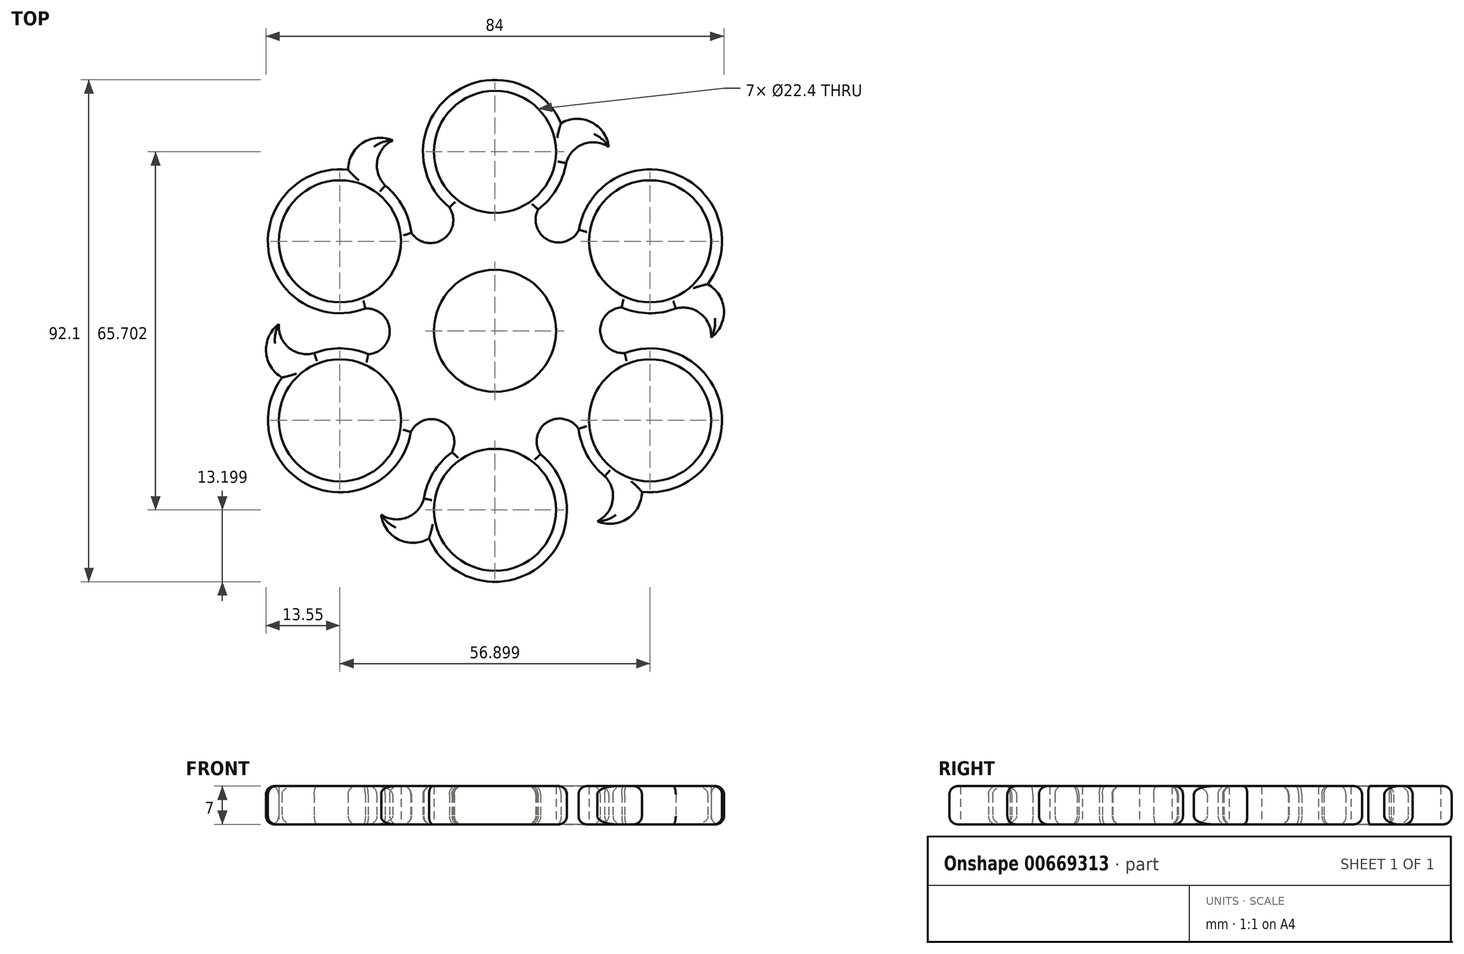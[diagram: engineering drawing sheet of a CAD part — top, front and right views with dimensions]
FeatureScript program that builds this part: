
annotation { "Feature Type Name" : "Feature", "Feature Type Description" : "" }
export const myFeature = defineFeature(function(context is Context, id is Id, definition is map)
    precondition{}
    {
        {
            var Q0;
            Q0=qCreatedBy(makeId("Top.planeOp"),FACE);
            var sketch = newSketch(context, id + "F0", { "sketchPlane" : qUnion([Q0])});
            skCircle(sketch, "E0", {"center": v(0, 0) * mm, "radius": 11.2 * mm});
            skCircle(sketch, "E1", {"center": v(0, 0) * mm, "radius": 13.2 * mm});
            skCircle(sketch, "E2", {"center": v(0, 32.85) * mm, "radius": 11.2 * mm});
            skCircle(sketch, "E3", {"center": v(0, 32.85) * mm, "radius": 13.2 * mm});
            skCircle(sketch, "E4.1.0", {"center": v(-28.45, 16.43) * mm, "radius": 11.2 * mm});
            skCircle(sketch, "E4.1.1", {"center": v(-28.45, 16.43) * mm, "radius": 13.2 * mm});
            skCircle(sketch, "E4.2.0", {"center": v(-28.45, -16.43) * mm, "radius": 11.2 * mm});
            skCircle(sketch, "E4.2.1", {"center": v(-28.45, -16.43) * mm, "radius": 13.2 * mm});
            skCircle(sketch, "E4.3.0", {"center": v(0, -32.85) * mm, "radius": 11.2 * mm});
            skCircle(sketch, "E4.3.1", {"center": v(0, -32.85) * mm, "radius": 13.2 * mm});
            skCircle(sketch, "E4.4.0", {"center": v(28.45, -16.43) * mm, "radius": 11.2 * mm});
            skCircle(sketch, "E4.4.1", {"center": v(28.45, -16.43) * mm, "radius": 13.2 * mm});
            skCircle(sketch, "E4.5.0", {"center": v(28.45, 16.43) * mm, "radius": 11.2 * mm});
            skCircle(sketch, "E4.5.1", {"center": v(28.45, 16.43) * mm, "radius": 13.2 * mm});
            skArc(sketch, "E5", {"start": v(-15.34, 18) * mm, "mid": v(-9.52, 16.8) * mm, "end": v(-8.36, 22.64) * mm});
            skArc(sketch, "E6.1.0", {"start": v(-23.26, -4.3) * mm, "mid": v(-19.3, 0.16) * mm, "end": v(-23.79, 4.08) * mm});
            skArc(sketch, "E6.2.0", {"start": v(-7.91, -22.29) * mm, "mid": v(-9.8, -16.64) * mm, "end": v(-15.42, -18.56) * mm});
            skArc(sketch, "E6.3.0", {"start": v(15.34, -18) * mm, "mid": v(9.52, -16.8) * mm, "end": v(8.36, -22.64) * mm});
            skArc(sketch, "E6.4.0", {"start": v(23.26, 4.3) * mm, "mid": v(19.3, -0.16) * mm, "end": v(23.79, -4.08) * mm});
            skArc(sketch, "E6.5.0", {"start": v(7.91, 22.29) * mm, "mid": v(9.8, 16.64) * mm, "end": v(15.42, 18.56) * mm});
            skArc(sketch, "E7", {"start": v(20.88, 33.73) * mm, "mid": v(17.68, 38.28) * mm, "end": v(12.1, 38.1) * mm});
            skArc(sketch, "E8", {"start": v(20.88, 33.73) * mm, "mid": v(16.19, 34.28) * mm, "end": v(13.03, 30.76) * mm});
            skArc(sketch, "E9.1.0", {"start": v(-18.77, 34.94) * mm, "mid": v(-24.32, 34.45) * mm, "end": v(-26.94, 29.54) * mm});
            skArc(sketch, "E9.1.1", {"start": v(-18.77, 34.94) * mm, "mid": v(-21.6, 31.16) * mm, "end": v(-20.12, 26.67) * mm});
            skArc(sketch, "E9.2.0", {"start": v(-39.65, 1.22) * mm, "mid": v(-42, -3.83) * mm, "end": v(-39.05, -8.56) * mm});
            skArc(sketch, "E9.2.1", {"start": v(-39.65, 1.22) * mm, "mid": v(-37.78, -3.12) * mm, "end": v(-33.16, -4.1) * mm});
            skArc(sketch, "E9.3.0", {"start": v(-20.88, -33.73) * mm, "mid": v(-17.68, -38.28) * mm, "end": v(-12.1, -38.1) * mm});
            skArc(sketch, "E9.3.1", {"start": v(-20.88, -33.73) * mm, "mid": v(-16.19, -34.28) * mm, "end": v(-13.03, -30.76) * mm});
            skArc(sketch, "E9.4.0", {"start": v(18.77, -34.94) * mm, "mid": v(24.32, -34.45) * mm, "end": v(26.94, -29.54) * mm});
            skArc(sketch, "E9.4.1", {"start": v(18.77, -34.94) * mm, "mid": v(21.6, -31.16) * mm, "end": v(20.12, -26.67) * mm});
            skArc(sketch, "E9.5.0", {"start": v(39.65, -1.22) * mm, "mid": v(42, 3.83) * mm, "end": v(39.05, 8.56) * mm});
            skArc(sketch, "E9.5.1", {"start": v(39.65, -1.22) * mm, "mid": v(37.78, 3.12) * mm, "end": v(33.16, 4.1) * mm});
            skSolve(sketch);
        }
        {
            var Q0;
            Q0=makeQuery(id+"F0.imprint","IMPRINT",FACE,{"disambiguationData":[TD([[makeQuery(id+"F0.imprint","IMPRINT",EDGE,{"derivedFrom":sQuery(id+"F0.wireOp",EDGE,"E1")}),-1.0]])]});
            var Q1;
            Q1=makeQuery(id+"F0.imprint","IMPRINT",FACE,{"disambiguationData":[TD([[makeQuery(id+"F0.imprint","IMPRINT",EDGE,{"derivedFrom":sQuery(id+"F0.wireOp",EDGE,"E0")}),-1.0]])]});
            var Q2;
            Q2=makeQuery(id+"F0.imprint","IMPRINT",FACE,{"disambiguationData":[TD([[makeQuery(id+"F0.imprint","IMPRINT",EDGE,{"derivedFrom":sQuery(id+"F0.wireOp",EDGE,"E4.5.0")}),-1.0]])]});
            var Q3;
            {var subQ0=sQuery(id+"F0.wireOp",EDGE,"E9.5.0");Q3=makeQuery(id+"F0.imprint","IMPRINT",FACE,{"disambiguationData":[TD([[makeQuery(id+"F0.imprint","IMPRINT",EDGE,{"derivedFrom":subQ0}),1.0]])]});}
            var Q4;
            {var subQ0=sQuery(id+"F0.wireOp",EDGE,"E7");Q4=makeQuery(id+"F0.imprint","IMPRINT",FACE,{"disambiguationData":[TD([[makeQuery(id+"F0.imprint","IMPRINT",EDGE,{"derivedFrom":subQ0}),1.0]])]});}
            var Q5;
            {var subQ0=sQuery(id+"F0.wireOp",EDGE,"E9.1.0");Q5=makeQuery(id+"F0.imprint","IMPRINT",FACE,{"disambiguationData":[TD([[makeQuery(id+"F0.imprint","IMPRINT",EDGE,{"derivedFrom":subQ0}),1.0]])]});}
            var Q6;
            {var subQ0=sQuery(id+"F0.wireOp",EDGE,"E9.2.0");Q6=makeQuery(id+"F0.imprint","IMPRINT",FACE,{"disambiguationData":[TD([[makeQuery(id+"F0.imprint","IMPRINT",EDGE,{"derivedFrom":subQ0}),1.0]])]});}
            var Q7;
            {var subQ0=sQuery(id+"F0.wireOp",EDGE,"E9.3.0");Q7=makeQuery(id+"F0.imprint","IMPRINT",FACE,{"disambiguationData":[TD([[makeQuery(id+"F0.imprint","IMPRINT",EDGE,{"derivedFrom":subQ0}),1.0]])]});}
            var Q8;
            Q8=makeQuery(id+"F0.imprint","IMPRINT",FACE,{"disambiguationData":[TD([[makeQuery(id+"F0.imprint","IMPRINT",EDGE,{"derivedFrom":sQuery(id+"F0.wireOp",EDGE,"E4.3.0")}),-1.0]])]});
            var Q9;
            {var subQ0=sQuery(id+"F0.wireOp",EDGE,"E9.4.0");Q9=makeQuery(id+"F0.imprint","IMPRINT",FACE,{"disambiguationData":[TD([[makeQuery(id+"F0.imprint","IMPRINT",EDGE,{"derivedFrom":subQ0}),1.0]])]});}
            var Q10;
            Q10=makeQuery(id+"F0.imprint","IMPRINT",FACE,{"disambiguationData":[TD([[makeQuery(id+"F0.imprint","IMPRINT",EDGE,{"derivedFrom":sQuery(id+"F0.wireOp",EDGE,"E4.4.0")}),-1.0]])]});
            var Q11;
            Q11=makeQuery(id+"F0.imprint","IMPRINT",FACE,{"disambiguationData":[TD([[makeQuery(id+"F0.imprint","IMPRINT",EDGE,{"derivedFrom":sQuery(id+"F0.wireOp",EDGE,"E4.2.0")}),-1.0]])]});
            var Q12;
            Q12=makeQuery(id+"F0.imprint","IMPRINT",FACE,{"disambiguationData":[TD([[makeQuery(id+"F0.imprint","IMPRINT",EDGE,{"derivedFrom":sQuery(id+"F0.wireOp",EDGE,"E4.1.0")}),-1.0]])]});
            var Q13;
            Q13=makeQuery(id+"F0.imprint","IMPRINT",FACE,{"disambiguationData":[TD([[makeQuery(id+"F0.imprint","IMPRINT",EDGE,{"derivedFrom":sQuery(id+"F0.wireOp",EDGE,"E2")}),-1.0]])]});
            extrude(context, id + "F1", {"entities" : qUnion([Q0, Q1, Q2, Q3, Q4, Q5, Q6, Q7, Q8, Q9, Q10, Q11, Q12, Q13]), "depth" : 7 * mm, "offsetDistance" : 25 * mm});
        }
        {
            var Q0;
            {var subQ0=sQuery(id+"F0.wireOp",EDGE,"E4.3.1");Q0=makeQuery(id+"F1.opExtrude","CAP_EDGE",EDGE,{"disambiguationData":[OSD([subQ0]),TDD([makeQuery(id+"F0.imprint","IMPRINT",EDGE,{"disambiguationData":[TD([[makeQuery(id+"F0.imprint","INTERSECT",VERTEX,{"derivedFrom":[subQ0,sQuery(id+"F0.wireOp",EDGE,"E6.3.0")]}),1.0]])],"derivedFrom":subQ0})])],"isStart":false});}
            var Q1;
            Q1=makeQuery(id+"F1.opExtrude","CAP_EDGE",EDGE,{"disambiguationData":[OSD([sQuery(id+"F0.wireOp",EDGE,"E9.3.0")])],"isStart":false});
            var Q2;
            Q2=makeQuery(id+"F1.opExtrude","CAP_EDGE",EDGE,{"disambiguationData":[OSD([sQuery(id+"F0.wireOp",EDGE,"E9.3.1")])],"isStart":false});
            var Q3;
            {var subQ0=sQuery(id+"F0.wireOp",EDGE,"E4.3.1");Q3=makeQuery(id+"F1.opExtrude","CAP_EDGE",EDGE,{"disambiguationData":[OSD([subQ0]),TDD([makeQuery(id+"F0.imprint","IMPRINT",EDGE,{"disambiguationData":[TD([[makeQuery(id+"F0.imprint","INTERSECT",VERTEX,{"derivedFrom":[subQ0,sQuery(id+"F0.wireOp",EDGE,"E6.2.0")]}),-1.0]])],"derivedFrom":subQ0})])],"isStart":false});}
            var Q4;
            Q4=makeQuery(id+"F1.opExtrude","CAP_EDGE",EDGE,{"disambiguationData":[OSD([sQuery(id+"F0.wireOp",EDGE,"E6.2.0")])],"isStart":false});
            var Q5;
            {var subQ0=sQuery(id+"F0.wireOp",EDGE,"E4.2.1");Q5=makeQuery(id+"F1.opExtrude","CAP_EDGE",EDGE,{"disambiguationData":[OSD([subQ0]),TDD([makeQuery(id+"F0.imprint","IMPRINT",EDGE,{"disambiguationData":[TD([[makeQuery(id+"F0.imprint","INTERSECT",VERTEX,{"derivedFrom":[subQ0,sQuery(id+"F0.wireOp",EDGE,"E6.2.0")]}),1.0]])],"derivedFrom":subQ0})])],"isStart":false});}
            var Q6;
            Q6=makeQuery(id+"F1.opExtrude","CAP_EDGE",EDGE,{"disambiguationData":[OSD([sQuery(id+"F0.wireOp",EDGE,"E9.2.0")])],"isStart":false});
            var Q7;
            {var subQ0=sQuery(id+"F0.wireOp",EDGE,"E4.1.1");Q7=makeQuery(id+"F1.opExtrude","CAP_EDGE",EDGE,{"disambiguationData":[OSD([subQ0]),TDD([makeQuery(id+"F0.imprint","IMPRINT",EDGE,{"disambiguationData":[TD([[makeQuery(id+"F0.imprint","INTERSECT",VERTEX,{"derivedFrom":[subQ0,sQuery(id+"F0.wireOp",EDGE,"E6.1.0")]}),1.0]])],"derivedFrom":subQ0})])],"isStart":false});}
            var Q8;
            {var subQ0=sQuery(id+"F0.wireOp",EDGE,"E4.2.1");Q8=makeQuery(id+"F1.opExtrude","CAP_EDGE",EDGE,{"disambiguationData":[OSD([subQ0]),TDD([makeQuery(id+"F0.imprint","IMPRINT",EDGE,{"disambiguationData":[TD([[makeQuery(id+"F0.imprint","INTERSECT",VERTEX,{"derivedFrom":[subQ0,sQuery(id+"F0.wireOp",EDGE,"E6.1.0")]}),-1.0]])],"derivedFrom":subQ0})])],"isStart":false});}
            var Q9;
            Q9=makeQuery(id+"F1.opExtrude","CAP_EDGE",EDGE,{"disambiguationData":[OSD([sQuery(id+"F0.wireOp",EDGE,"E9.2.1")])],"isStart":false});
            var Q10;
            Q10=makeQuery(id+"F1.opExtrude","CAP_EDGE",EDGE,{"disambiguationData":[OSD([sQuery(id+"F0.wireOp",EDGE,"E6.1.0")])],"isStart":false});
            var Q11;
            Q11=makeQuery(id+"F1.opExtrude","CAP_EDGE",EDGE,{"disambiguationData":[OSD([sQuery(id+"F0.wireOp",EDGE,"E9.1.0")])],"isStart":false});
            var Q12;
            Q12=makeQuery(id+"F1.opExtrude","CAP_EDGE",EDGE,{"disambiguationData":[OSD([sQuery(id+"F0.wireOp",EDGE,"E9.1.1")])],"isStart":false});
            var Q13;
            {var subQ0=sQuery(id+"F0.wireOp",EDGE,"E4.1.1");Q13=makeQuery(id+"F1.opExtrude","CAP_EDGE",EDGE,{"disambiguationData":[OSD([subQ0]),TDD([makeQuery(id+"F0.imprint","IMPRINT",EDGE,{"disambiguationData":[TD([[makeQuery(id+"F0.imprint","INTERSECT",VERTEX,{"derivedFrom":[subQ0,sQuery(id+"F0.wireOp",EDGE,"E5")]}),-1.0]])],"derivedFrom":subQ0})])],"isStart":false});}
            var Q14;
            Q14=makeQuery(id+"F1.opExtrude","CAP_EDGE",EDGE,{"disambiguationData":[OSD([sQuery(id+"F0.wireOp",EDGE,"E5")])],"isStart":false});
            var Q15;
            {var subQ0=sQuery(id+"F0.wireOp",EDGE,"E3");Q15=makeQuery(id+"F1.opExtrude","CAP_EDGE",EDGE,{"disambiguationData":[OSD([subQ0]),TDD([makeQuery(id+"F0.imprint","IMPRINT",EDGE,{"disambiguationData":[TD([[makeQuery(id+"F0.imprint","INTERSECT",VERTEX,{"derivedFrom":[subQ0,sQuery(id+"F0.wireOp",EDGE,"E5")]}),1.0]])],"derivedFrom":subQ0})])],"isStart":false});}
            var Q16;
            Q16=makeQuery(id+"F1.opExtrude","CAP_EDGE",EDGE,{"disambiguationData":[OSD([sQuery(id+"F0.wireOp",EDGE,"E7")])],"isStart":false});
            var Q17;
            Q17=makeQuery(id+"F1.opExtrude","CAP_EDGE",EDGE,{"disambiguationData":[OSD([sQuery(id+"F0.wireOp",EDGE,"E8")])],"isStart":false});
            var Q18;
            {var subQ0=sQuery(id+"F0.wireOp",EDGE,"E3");Q18=makeQuery(id+"F1.opExtrude","CAP_EDGE",EDGE,{"disambiguationData":[OSD([subQ0]),TDD([makeQuery(id+"F0.imprint","IMPRINT",EDGE,{"disambiguationData":[TD([[makeQuery(id+"F0.imprint","INTERSECT",VERTEX,{"derivedFrom":[subQ0,sQuery(id+"F0.wireOp",EDGE,"E6.5.0")]}),-1.0]])],"derivedFrom":subQ0})])],"isStart":false});}
            var Q19;
            Q19=makeQuery(id+"F1.opExtrude","CAP_EDGE",EDGE,{"disambiguationData":[OSD([sQuery(id+"F0.wireOp",EDGE,"E6.5.0")])],"isStart":false});
            var Q20;
            {var subQ0=sQuery(id+"F0.wireOp",EDGE,"E4.5.1");Q20=makeQuery(id+"F1.opExtrude","CAP_EDGE",EDGE,{"disambiguationData":[OSD([subQ0]),TDD([makeQuery(id+"F0.imprint","IMPRINT",EDGE,{"disambiguationData":[TD([[makeQuery(id+"F0.imprint","INTERSECT",VERTEX,{"derivedFrom":[subQ0,sQuery(id+"F0.wireOp",EDGE,"E6.5.0")]}),1.0]])],"derivedFrom":subQ0})])],"isStart":false});}
            var Q21;
            Q21=makeQuery(id+"F1.opExtrude","CAP_EDGE",EDGE,{"disambiguationData":[OSD([sQuery(id+"F0.wireOp",EDGE,"E9.5.0")])],"isStart":false});
            var Q22;
            Q22=makeQuery(id+"F1.opExtrude","CAP_EDGE",EDGE,{"disambiguationData":[OSD([sQuery(id+"F0.wireOp",EDGE,"E9.5.1")])],"isStart":false});
            var Q23;
            {var subQ0=sQuery(id+"F0.wireOp",EDGE,"E4.5.1");Q23=makeQuery(id+"F1.opExtrude","CAP_EDGE",EDGE,{"disambiguationData":[OSD([subQ0]),TDD([makeQuery(id+"F0.imprint","IMPRINT",EDGE,{"disambiguationData":[TD([[makeQuery(id+"F0.imprint","INTERSECT",VERTEX,{"derivedFrom":[subQ0,sQuery(id+"F0.wireOp",EDGE,"E6.4.0")]}),-1.0]])],"derivedFrom":subQ0})])],"isStart":false});}
            var Q24;
            Q24=makeQuery(id+"F1.opExtrude","CAP_EDGE",EDGE,{"disambiguationData":[OSD([sQuery(id+"F0.wireOp",EDGE,"E6.4.0")])],"isStart":false});
            var Q25;
            {var subQ0=sQuery(id+"F0.wireOp",EDGE,"E4.4.1");Q25=makeQuery(id+"F1.opExtrude","CAP_EDGE",EDGE,{"disambiguationData":[OSD([subQ0]),TDD([makeQuery(id+"F0.imprint","IMPRINT",EDGE,{"disambiguationData":[TD([[makeQuery(id+"F0.imprint","INTERSECT",VERTEX,{"derivedFrom":[subQ0,sQuery(id+"F0.wireOp",EDGE,"E6.4.0")]}),1.0]])],"derivedFrom":subQ0})])],"isStart":false});}
            var Q26;
            Q26=makeQuery(id+"F1.opExtrude","CAP_EDGE",EDGE,{"disambiguationData":[OSD([sQuery(id+"F0.wireOp",EDGE,"E9.4.0")])],"isStart":false});
            var Q27;
            Q27=makeQuery(id+"F1.opExtrude","CAP_EDGE",EDGE,{"disambiguationData":[OSD([sQuery(id+"F0.wireOp",EDGE,"E6.3.0")])],"isStart":false});
            var Q28;
            {var subQ0=sQuery(id+"F0.wireOp",EDGE,"E4.4.1");Q28=makeQuery(id+"F1.opExtrude","CAP_EDGE",EDGE,{"disambiguationData":[OSD([subQ0]),TDD([makeQuery(id+"F0.imprint","IMPRINT",EDGE,{"disambiguationData":[TD([[makeQuery(id+"F0.imprint","INTERSECT",VERTEX,{"derivedFrom":[subQ0,sQuery(id+"F0.wireOp",EDGE,"E6.3.0")]}),-1.0]])],"derivedFrom":subQ0})])],"isStart":false});}
            var Q29;
            Q29=makeQuery(id+"F1.opExtrude","CAP_EDGE",EDGE,{"disambiguationData":[OSD([sQuery(id+"F0.wireOp",EDGE,"E9.4.1")])],"isStart":false});
            fillet(context, id + "F2", {"entities" : qUnion([Q0, Q1, Q2, Q3, Q4, Q5, Q6, Q7, Q8, Q9, Q10, Q11, Q12, Q13, Q14, Q15, Q16, Q17, Q18, Q19, Q20, Q21, Q22, Q23, Q24, Q25, Q26, Q27, Q28, Q29]), "radius" : 1.5 * mm, "tangentPropagation" : true, "allowEdgeOverflow" : false});
        }
        {
            var Q0;
            {var subQ0=sQuery(id+"F0.wireOp",EDGE,"E4.2.1");Q0=makeQuery(id+"F1.opExtrude","CAP_EDGE",EDGE,{"disambiguationData":[OSD([subQ0]),TDD([makeQuery(id+"F0.imprint","IMPRINT",EDGE,{"disambiguationData":[TD([[makeQuery(id+"F0.imprint","INTERSECT",VERTEX,{"derivedFrom":[subQ0,sQuery(id+"F0.wireOp",EDGE,"E6.2.0")]}),1.0]])],"derivedFrom":subQ0})])],"isStart":true});}
            var Q1;
            Q1=makeQuery(id+"F1.opExtrude","CAP_EDGE",EDGE,{"disambiguationData":[OSD([sQuery(id+"F0.wireOp",EDGE,"E9.2.0")])],"isStart":true});
            var Q2;
            {var subQ0=sQuery(id+"F0.wireOp",EDGE,"E4.2.1");Q2=makeQuery(id+"F1.opExtrude","CAP_EDGE",EDGE,{"disambiguationData":[OSD([subQ0]),TDD([makeQuery(id+"F0.imprint","IMPRINT",EDGE,{"disambiguationData":[TD([[makeQuery(id+"F0.imprint","INTERSECT",VERTEX,{"derivedFrom":[subQ0,sQuery(id+"F0.wireOp",EDGE,"E6.1.0")]}),-1.0]])],"derivedFrom":subQ0})])],"isStart":true});}
            var Q3;
            Q3=makeQuery(id+"F1.opExtrude","CAP_EDGE",EDGE,{"disambiguationData":[OSD([sQuery(id+"F0.wireOp",EDGE,"E9.2.1")])],"isStart":true});
            var Q4;
            Q4=makeQuery(id+"F1.opExtrude","CAP_EDGE",EDGE,{"disambiguationData":[OSD([sQuery(id+"F0.wireOp",EDGE,"E6.1.0")])],"isStart":true});
            var Q5;
            {var subQ0=sQuery(id+"F0.wireOp",EDGE,"E4.1.1");Q5=makeQuery(id+"F1.opExtrude","CAP_EDGE",EDGE,{"disambiguationData":[OSD([subQ0]),TDD([makeQuery(id+"F0.imprint","IMPRINT",EDGE,{"disambiguationData":[TD([[makeQuery(id+"F0.imprint","INTERSECT",VERTEX,{"derivedFrom":[subQ0,sQuery(id+"F0.wireOp",EDGE,"E6.1.0")]}),1.0]])],"derivedFrom":subQ0})])],"isStart":true});}
            var Q6;
            Q6=makeQuery(id+"F1.opExtrude","CAP_EDGE",EDGE,{"disambiguationData":[OSD([sQuery(id+"F0.wireOp",EDGE,"E9.1.0")])],"isStart":true});
            var Q7;
            Q7=makeQuery(id+"F1.opExtrude","CAP_EDGE",EDGE,{"disambiguationData":[OSD([sQuery(id+"F0.wireOp",EDGE,"E9.1.1")])],"isStart":true});
            var Q8;
            {var subQ0=sQuery(id+"F0.wireOp",EDGE,"E4.1.1");Q8=makeQuery(id+"F1.opExtrude","CAP_EDGE",EDGE,{"disambiguationData":[OSD([subQ0]),TDD([makeQuery(id+"F0.imprint","IMPRINT",EDGE,{"disambiguationData":[TD([[makeQuery(id+"F0.imprint","INTERSECT",VERTEX,{"derivedFrom":[subQ0,sQuery(id+"F0.wireOp",EDGE,"E5")]}),-1.0]])],"derivedFrom":subQ0})])],"isStart":true});}
            var Q9;
            Q9=makeQuery(id+"F1.opExtrude","CAP_EDGE",EDGE,{"disambiguationData":[OSD([sQuery(id+"F0.wireOp",EDGE,"E5")])],"isStart":true});
            var Q10;
            {var subQ0=sQuery(id+"F0.wireOp",EDGE,"E3");Q10=makeQuery(id+"F1.opExtrude","CAP_EDGE",EDGE,{"disambiguationData":[OSD([subQ0]),TDD([makeQuery(id+"F0.imprint","IMPRINT",EDGE,{"disambiguationData":[TD([[makeQuery(id+"F0.imprint","INTERSECT",VERTEX,{"derivedFrom":[subQ0,sQuery(id+"F0.wireOp",EDGE,"E5")]}),1.0]])],"derivedFrom":subQ0})])],"isStart":true});}
            var Q11;
            Q11=makeQuery(id+"F1.opExtrude","CAP_EDGE",EDGE,{"disambiguationData":[OSD([sQuery(id+"F0.wireOp",EDGE,"E7")])],"isStart":true});
            var Q12;
            Q12=makeQuery(id+"F1.opExtrude","CAP_EDGE",EDGE,{"disambiguationData":[OSD([sQuery(id+"F0.wireOp",EDGE,"E8")])],"isStart":true});
            var Q13;
            {var subQ0=sQuery(id+"F0.wireOp",EDGE,"E3");Q13=makeQuery(id+"F1.opExtrude","CAP_EDGE",EDGE,{"disambiguationData":[OSD([subQ0]),TDD([makeQuery(id+"F0.imprint","IMPRINT",EDGE,{"disambiguationData":[TD([[makeQuery(id+"F0.imprint","INTERSECT",VERTEX,{"derivedFrom":[subQ0,sQuery(id+"F0.wireOp",EDGE,"E6.5.0")]}),-1.0]])],"derivedFrom":subQ0})])],"isStart":true});}
            var Q14;
            Q14=makeQuery(id+"F1.opExtrude","CAP_EDGE",EDGE,{"disambiguationData":[OSD([sQuery(id+"F0.wireOp",EDGE,"E6.5.0")])],"isStart":true});
            var Q15;
            {var subQ0=sQuery(id+"F0.wireOp",EDGE,"E4.5.1");Q15=makeQuery(id+"F1.opExtrude","CAP_EDGE",EDGE,{"disambiguationData":[OSD([subQ0]),TDD([makeQuery(id+"F0.imprint","IMPRINT",EDGE,{"disambiguationData":[TD([[makeQuery(id+"F0.imprint","INTERSECT",VERTEX,{"derivedFrom":[subQ0,sQuery(id+"F0.wireOp",EDGE,"E6.5.0")]}),1.0]])],"derivedFrom":subQ0})])],"isStart":true});}
            var Q16;
            Q16=makeQuery(id+"F1.opExtrude","CAP_EDGE",EDGE,{"disambiguationData":[OSD([sQuery(id+"F0.wireOp",EDGE,"E9.5.0")])],"isStart":true});
            var Q17;
            {var subQ0=sQuery(id+"F0.wireOp",EDGE,"E4.5.1");Q17=makeQuery(id+"F1.opExtrude","CAP_EDGE",EDGE,{"disambiguationData":[OSD([subQ0]),TDD([makeQuery(id+"F0.imprint","IMPRINT",EDGE,{"disambiguationData":[TD([[makeQuery(id+"F0.imprint","INTERSECT",VERTEX,{"derivedFrom":[subQ0,sQuery(id+"F0.wireOp",EDGE,"E6.4.0")]}),-1.0]])],"derivedFrom":subQ0})])],"isStart":true});}
            var Q18;
            Q18=makeQuery(id+"F1.opExtrude","CAP_EDGE",EDGE,{"disambiguationData":[OSD([sQuery(id+"F0.wireOp",EDGE,"E9.5.1")])],"isStart":true});
            var Q19;
            Q19=makeQuery(id+"F1.opExtrude","CAP_EDGE",EDGE,{"disambiguationData":[OSD([sQuery(id+"F0.wireOp",EDGE,"E6.4.0")])],"isStart":true});
            var Q20;
            {var subQ0=sQuery(id+"F0.wireOp",EDGE,"E4.4.1");Q20=makeQuery(id+"F1.opExtrude","CAP_EDGE",EDGE,{"disambiguationData":[OSD([subQ0]),TDD([makeQuery(id+"F0.imprint","IMPRINT",EDGE,{"disambiguationData":[TD([[makeQuery(id+"F0.imprint","INTERSECT",VERTEX,{"derivedFrom":[subQ0,sQuery(id+"F0.wireOp",EDGE,"E6.4.0")]}),1.0]])],"derivedFrom":subQ0})])],"isStart":true});}
            var Q21;
            Q21=makeQuery(id+"F1.opExtrude","CAP_EDGE",EDGE,{"disambiguationData":[OSD([sQuery(id+"F0.wireOp",EDGE,"E9.4.0")])],"isStart":true});
            var Q22;
            Q22=makeQuery(id+"F1.opExtrude","CAP_EDGE",EDGE,{"disambiguationData":[OSD([sQuery(id+"F0.wireOp",EDGE,"E9.4.1")])],"isStart":true});
            var Q23;
            {var subQ0=sQuery(id+"F0.wireOp",EDGE,"E4.4.1");Q23=makeQuery(id+"F1.opExtrude","CAP_EDGE",EDGE,{"disambiguationData":[OSD([subQ0]),TDD([makeQuery(id+"F0.imprint","IMPRINT",EDGE,{"disambiguationData":[TD([[makeQuery(id+"F0.imprint","INTERSECT",VERTEX,{"derivedFrom":[subQ0,sQuery(id+"F0.wireOp",EDGE,"E6.3.0")]}),-1.0]])],"derivedFrom":subQ0})])],"isStart":true});}
            var Q24;
            Q24=makeQuery(id+"F1.opExtrude","CAP_EDGE",EDGE,{"disambiguationData":[OSD([sQuery(id+"F0.wireOp",EDGE,"E6.3.0")])],"isStart":true});
            var Q25;
            {var subQ0=sQuery(id+"F0.wireOp",EDGE,"E4.3.1");Q25=makeQuery(id+"F1.opExtrude","CAP_EDGE",EDGE,{"disambiguationData":[OSD([subQ0]),TDD([makeQuery(id+"F0.imprint","IMPRINT",EDGE,{"disambiguationData":[TD([[makeQuery(id+"F0.imprint","INTERSECT",VERTEX,{"derivedFrom":[subQ0,sQuery(id+"F0.wireOp",EDGE,"E6.3.0")]}),1.0]])],"derivedFrom":subQ0})])],"isStart":true});}
            var Q26;
            Q26=makeQuery(id+"F1.opExtrude","CAP_EDGE",EDGE,{"disambiguationData":[OSD([sQuery(id+"F0.wireOp",EDGE,"E9.3.0")])],"isStart":true});
            var Q27;
            {var subQ0=sQuery(id+"F0.wireOp",EDGE,"E4.3.1");Q27=makeQuery(id+"F1.opExtrude","CAP_EDGE",EDGE,{"disambiguationData":[OSD([subQ0]),TDD([makeQuery(id+"F0.imprint","IMPRINT",EDGE,{"disambiguationData":[TD([[makeQuery(id+"F0.imprint","INTERSECT",VERTEX,{"derivedFrom":[subQ0,sQuery(id+"F0.wireOp",EDGE,"E6.2.0")]}),-1.0]])],"derivedFrom":subQ0})])],"isStart":true});}
            var Q28;
            Q28=makeQuery(id+"F1.opExtrude","CAP_EDGE",EDGE,{"disambiguationData":[OSD([sQuery(id+"F0.wireOp",EDGE,"E9.3.1")])],"isStart":true});
            var Q29;
            Q29=makeQuery(id+"F1.opExtrude","CAP_EDGE",EDGE,{"disambiguationData":[OSD([sQuery(id+"F0.wireOp",EDGE,"E6.2.0")])],"isStart":true});
            fillet(context, id + "F3", {"entities" : qUnion([Q0, Q1, Q2, Q3, Q4, Q5, Q6, Q7, Q8, Q9, Q10, Q11, Q12, Q13, Q14, Q15, Q16, Q17, Q18, Q19, Q20, Q21, Q22, Q23, Q24, Q25, Q26, Q27, Q28, Q29]), "radius" : 1.5 * mm, "tangentPropagation" : true, "allowEdgeOverflow" : false});
        }
    });
